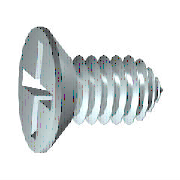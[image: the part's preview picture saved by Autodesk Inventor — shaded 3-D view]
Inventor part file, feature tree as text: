
AUTODESK INVENTOR PART (.ipt)
format: ipt  version: 2020 (Build 240168000, 168)  size: 235,008 bytes
history: native  units: mm (DEFAULTED — no unit token found)
features: sketch x2, extrude x1, plane x1
ambient origin geometry x8: Origin, YZ Plane, XZ Plane, XY Plane, X Axis, Y Axis, Z Axis, Center Point
bodies: Solid1 (feature_tree), Body (feature_tree)
feature tree (4):
  sketch  "Sketch1"  dims[d0=19.0mm d1=2.8mm d2=4.8mm d3=9.3mm]
  sketch  "Sketch2"  dims[d8=90.0deg d4=3.2mm d5=5.2mm d6=4.625123mm d7=10.821041mm d9=16.2mm d10=0.0mm d11=2.4mm d12=4.3mm d13=45.0deg d14=2.8mm d15=19.0mm d45=3.2mm d16=0.174533mm d17=5.2mm d18=45.0deg d19=1.56mm d20=1.82mm d21=5.2mm d22=0.33mm d24=0.0mm d25=0.132mm d62=45.0deg d64=0.0mm d65=0.0mm]
  extrude  "Slot"  Depth=9.3mm
  plane  "Work Plane2"
